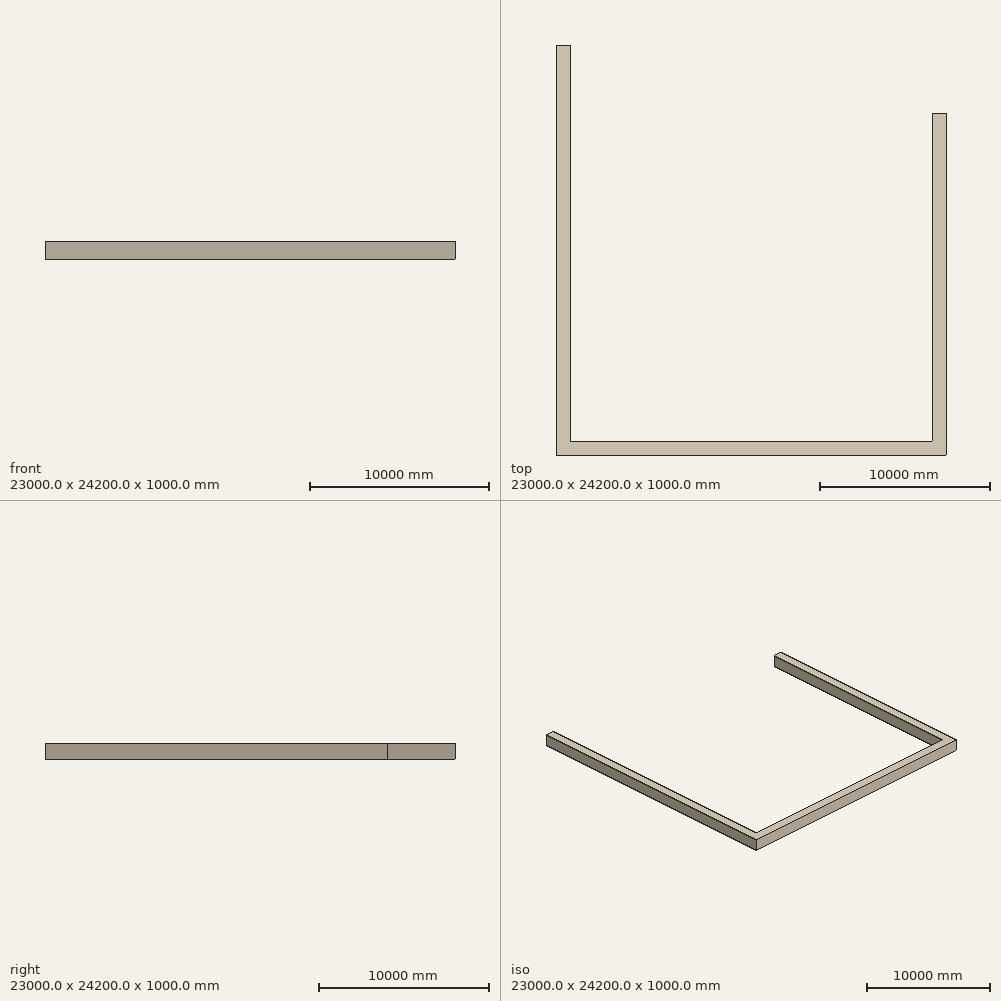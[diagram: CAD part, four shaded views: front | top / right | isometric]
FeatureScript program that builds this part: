
annotation { "Feature Type Name" : "Feature", "Feature Type Description" : "" }
export const myFeature = defineFeature(function(context is Context, id is Id, definition is map)
    precondition{}
    {
        {
            var Q0;
            Q0=qCreatedBy(makeId("Top.planeOp"),FACE);
            var sketch = newSketch(context, id + "F0", { "sketchPlane" : qUnion([Q0])});
            skPoint(sketch, "E0.middle", {"position": v(0, 0) * mm});
            skLineSegment(sketch, "E1.bottom", {"start": v(11500, 12500) * mm, "end": v(-11500, 12500) * mm});
            skLineSegment(sketch, "E1.top", {"start": v(11500, -12500) * mm, "end": v(-11500, -12500) * mm});
            skLineSegment(sketch, "E1.left", {"start": v(11500, 12500) * mm, "end": v(11500, -12500) * mm});
            skLineSegment(sketch, "E1.right", {"start": v(-11500, 12500) * mm, "end": v(-11500, -12500) * mm});
            skSolve(sketch);
        }
        {
            var Q0;
            Q0 = qSketchRegion(id + "F0", true);
            extrude(context, id + "F1", {"entities" : qUnion([Q0]), "depth" : 1000 * mm, "offsetDistance" : 25 * mm});
        }
        {
            var Q0;
            Q0=makeQuery(id+"F1.opExtrude","CAP_FACE",FACE,{"disambiguationData":[OSD([sQuery(id+"F0.wireOp",EDGE,"E1.bottom"),sQuery(id+"F0.wireOp",EDGE,"E1.top"),sQuery(id+"F0.wireOp",EDGE,"E1.left"),sQuery(id+"F0.wireOp",EDGE,"E1.right")])],"isStart":false});
            var sketch = newSketch(context, id + "F2", { "sketchPlane" : qUnion([Q0])});
            skLineSegment(sketch, "E2.bottom", {"start": v(10700, 11700) * mm, "end": v(-10700, 11700) * mm});
            skLineSegment(sketch, "E2.top", {"start": v(10700, -11700) * mm, "end": v(-10700, -11700) * mm});
            skLineSegment(sketch, "E2.left", {"start": v(10700, 11700) * mm, "end": v(10700, -11700) * mm});
            skLineSegment(sketch, "E2.right", {"start": v(-10700, 11700) * mm, "end": v(-10700, -11700) * mm});
            skPoint(sketch, "E2.middle", {"position": v(0, 0) * mm});
            skSolve(sketch);
        }
        {
            var Q0;
            Q0=makeQuery(id+"F2.imprint","IMPRINT",FACE,{"disambiguationData":[TD([[makeQuery(id+"F2.imprint","IMPRINT",EDGE,{"derivedFrom":sQuery(id+"F2.wireOp",EDGE,"E2.bottom")}),1.0]])]});
            extrude(context, id + "F3", {"entities" : qUnion([Q0]), "operationType" : NewBodyOperationType.REMOVE, "oppositeDirection" : true, "depth" : 1000 * mm, "offsetDistance" : 25 * mm});
        }
        {
            var Q0;
            Q0=makeQuery(id+"F1.opExtrude","CAP_FACE",FACE,{"disambiguationData":[OSD([sQuery(id+"F0.wireOp",EDGE,"E1.bottom"),sQuery(id+"F0.wireOp",EDGE,"E1.top"),sQuery(id+"F0.wireOp",EDGE,"E1.left"),sQuery(id+"F0.wireOp",EDGE,"E1.right")])],"isStart":false});
            var sketch = newSketch(context, id + "F4", { "sketchPlane" : qUnion([Q0])});
            skLineSegment(sketch, "E3.bottom", {"start": v(11500, 12500) * mm, "end": v(-11500, 12500) * mm});
            skLineSegment(sketch, "E3.top", {"start": v(11500, 11700) * mm, "end": v(-11500, 11700) * mm});
            skLineSegment(sketch, "E3.left", {"start": v(11500, 12500) * mm, "end": v(11500, 11700) * mm});
            skLineSegment(sketch, "E3.right", {"start": v(-11500, 12500) * mm, "end": v(-11500, 11700) * mm});
            skSolve(sketch);
        }
        {
            var Q0;
            Q0 = qSketchRegion(id + "F4", true);
            extrude(context, id + "F5", {"entities" : qUnion([Q0]), "operationType" : NewBodyOperationType.REMOVE, "oppositeDirection" : true, "depth" : 1000 * mm, "offsetDistance" : 25 * mm});
        }
        {
            var Q0;
            Q0=makeQuery(id+"F1.opExtrude","CAP_FACE",FACE,{"disambiguationData":[OSD([sQuery(id+"F0.wireOp",EDGE,"E1.bottom"),sQuery(id+"F0.wireOp",EDGE,"E1.top"),sQuery(id+"F0.wireOp",EDGE,"E1.left"),sQuery(id+"F0.wireOp",EDGE,"E1.right")])],"isStart":false});
            var sketch = newSketch(context, id + "F6", { "sketchPlane" : qUnion([Q0])});
            skLineSegment(sketch, "E4.bottom", {"start": v(10700, 11700) * mm, "end": v(11500, 11700) * mm});
            skLineSegment(sketch, "E4.top", {"start": v(10700, 11700) * mm, "end": v(11500, 11700) * mm});
            skLineSegment(sketch, "E4.left", {"start": v(10700, 11700) * mm, "end": v(10700, 11700) * mm});
            skLineSegment(sketch, "E4.right", {"start": v(11500, 11700) * mm, "end": v(11500, 11700) * mm});
            skLineSegment(sketch, "E5.bottom", {"start": v(11500, 7700) * mm, "end": v(10700, 7700) * mm});
            skLineSegment(sketch, "E5.top", {"start": v(11500, 11700) * mm, "end": v(10700, 11700) * mm});
            skLineSegment(sketch, "E5.left", {"start": v(11500, 7700) * mm, "end": v(11500, 11700) * mm});
            skLineSegment(sketch, "E5.right", {"start": v(10700, 7700) * mm, "end": v(10700, 11700) * mm});
            skSolve(sketch);
        }
        {
            var Q0;
            Q0 = qSketchRegion(id + "F6", true);
            extrude(context, id + "F7", {"entities" : qUnion([Q0]), "operationType" : NewBodyOperationType.REMOVE, "oppositeDirection" : true, "depth" : 1000 * mm, "offsetDistance" : 25 * mm});
        }
    });
